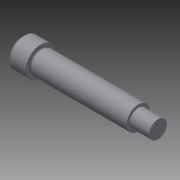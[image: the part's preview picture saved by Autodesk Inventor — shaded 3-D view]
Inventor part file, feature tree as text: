
AUTODESK INVENTOR PART (.ipt)
format: ipt  version: 2014 SP1 (Build 180222100, 222)  size: 101,888 bytes
history: native  units: in
note: dims shown in document units (in); Inventor stores cm internally (conversion verified against a paired STEP export)
features: revolve x1, chamfer x1, sketch x1
ambient origin geometry x8: Origin, YZ Plane, XZ Plane, XY Plane, X Axis, Y Axis, Z Axis, Center Point
bodies: Solid1 (feature_tree)
feature tree (3):
  revolve  "Revolution1"  [1 undecoded]
  chamfer  "Chamfer1"  Distance=0.124in
  sketch  "Sketch1"  dims[d0=0.647in d1=0.13in d2=0.124in d3=0.197in d4=0.156in d5=0.1165in d6=0.008in d7=90.0deg d8=0.02in d9=0.125in d10=45.0deg]
note: 1 required parameter value undecoded (feature->parameter linkage not recoverable at this tier; creation-order binding heuristic only, values carry confidence <= 0.55)
